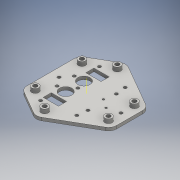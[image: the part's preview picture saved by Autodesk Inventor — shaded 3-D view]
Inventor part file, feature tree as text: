
AUTODESK INVENTOR PART (.ipt)
format: ipt  version: 2016 SP1 (Build 200210100, 210)  size: 498,688 bytes
history: native  units: mm
features: extrude x11, sketch x11, thread x6, projected_geometry x2, other x1, mirror x1, reference x1
ambient origin geometry x8: Origin, YZ Plane, XZ Plane, XY Plane, X Axis, Y Axis, Z Axis, Center Point
bodies: Solid1 (feature_tree)
feature tree (33):
  extrude  "Extrusion1"  Depth=12.0mm
  extrude  "Extrusion2"  Depth=4.0mm
  extrude  "Extrusion3"  Depth=23.0mm
  extrude  "Extrusion5"  Depth=3.0mm
  other  "Work Axis1"
  thread  "Thread1"  [1 undecoded]
  thread  "Thread2"  [1 undecoded]
  thread  "Thread3"  [1 undecoded]
  thread  "Thread4"  [1 undecoded]
  thread  "Thread5"  [1 undecoded]
  thread  "Thread6"  [1 undecoded]
  extrude  "Extrusion6"  Depth=3.0mm
  extrude  "Extrusion7"  Depth=17.0mm
  extrude  "Extrusion8"  Depth=5.0mm TaperAngle=0.0deg
  extrude  "Extrusion9"  Depth=3.0mm
  extrude  "Extrusion10"  Depth=14.0mm
  extrude  "Extrusion11"  Depth=5.0mm TaperAngle=0.0deg
  mirror  "Mirror1"
  extrude  "Extrusion12"  Depth=10.0mm
  sketch  "Sketch7"  dims[d21=3.0mm d23=21.0mm]
  sketch  "Sketch1"  dims[d0=12.0mm d1=12.0mm]
  sketch  "Sketch2"  dims[d4=4.0mm d5=4.0mm]
  sketch  "Sketch3"  dims[d6=46.0mm d7=23.0mm]
  sketch  "Sketch6"  dims[d8=28.0mm d9=28.0mm d10=12.0mm d11=12.0mm d13=30.0mm d15=360.0deg d17=5.0mm d18=0.0mm d19=3.0mm d20=3.0mm]
  reference  "Reference2"
  sketch  "Sketch8"  dims[d24=21.0mm d25=17.0mm]
  projected_geometry  "Projected Loop2"
  sketch  "Sketch9"  dims[d26=8.5mm d27=5.0mm d28=0.0mm]
  sketch  "Sketch10"  dims[d29=3.0mm d30=3.0mm]
  projected_geometry  "Projected Loop3"
  sketch  "Sketch12"  dims[d31=28.0mm d33=14.0mm]
  sketch  "Sketch13"  dims[d35=5.0mm d36=0.0mm d39=5.0mm d40=0.0mm]
  sketch  "Sketch14"  dims[d42=25.497423mm d45=9.0mm d46=9.0mm d47=9.0mm d48=22.0mm d49=22.0mm d50=10.0mm d51=0.0mm d52=10.0mm d53=0.0mm d54=10.0mm d55=0.0mm d56=10.0mm d57=0.0mm d58=10.0mm d59=0.0mm d60=10.0mm d61=0.0mm d62=1.5mm d63=1.5mm d64=1.5mm d65=1.5mm d66=1.5mm d67=1.5mm d68=2.0mm d69=0.0mm d70=2.0mm d71=0.0mm d72=2.0mm d73=2.0mm d74=0.0mm d75=0.0mm d76=0.0mm d77=25.0mm d78=25.0mm d79=2.0mm d80=0.0mm d84=8.0mm d85=15.0mm d86=2.0mm d87=2.0mm d88=0.0mm d89=3.0mm d90=8.5mm d91=30.0mm d93=360.0deg d95=10.0mm d96=0.0mm d97=8.5mm d98=0.0mm d99=30.0mm d101=360.0deg]
note: 6 required parameter values undecoded (feature->parameter linkage not recoverable at this tier; creation-order binding heuristic only, values carry confidence <= 0.55)
